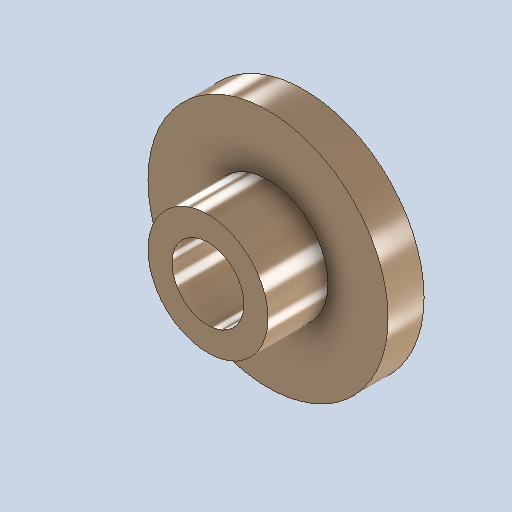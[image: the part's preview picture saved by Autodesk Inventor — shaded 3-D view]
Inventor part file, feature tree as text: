
AUTODESK INVENTOR PART (.ipt)
format: ipt  version: 2025.1 (Build 291241000, 241)  size: 273,920 bytes
history: native  units: mm
features: sketch x2, revolve x1, hole x1
ambient origin geometry x8: Origin, YZ Plane, XZ Plane, XY Plane, X Axis, Y Axis, Z Axis, Center Point
bodies: Solid1 (feature_tree)
feature tree (4):
  revolve  "Revolution1"  [1 undecoded]
  hole  "Hole1"  [1 undecoded]
  sketch  "Sketch1"  dims[d0=3.0mm d1=5.0mm]
  sketch  "Sketch2"  dims[d2=20.0mm d3=10.0mm d4=90.0deg d5=6.0mm d6=6.0mm d7=4.0mm d8=2.0mm d9=90.0deg d10=3.0mm d11=0.0mm]
note: 2 required parameter values undecoded (feature->parameter linkage not recoverable at this tier; creation-order binding heuristic only, values carry confidence <= 0.55)